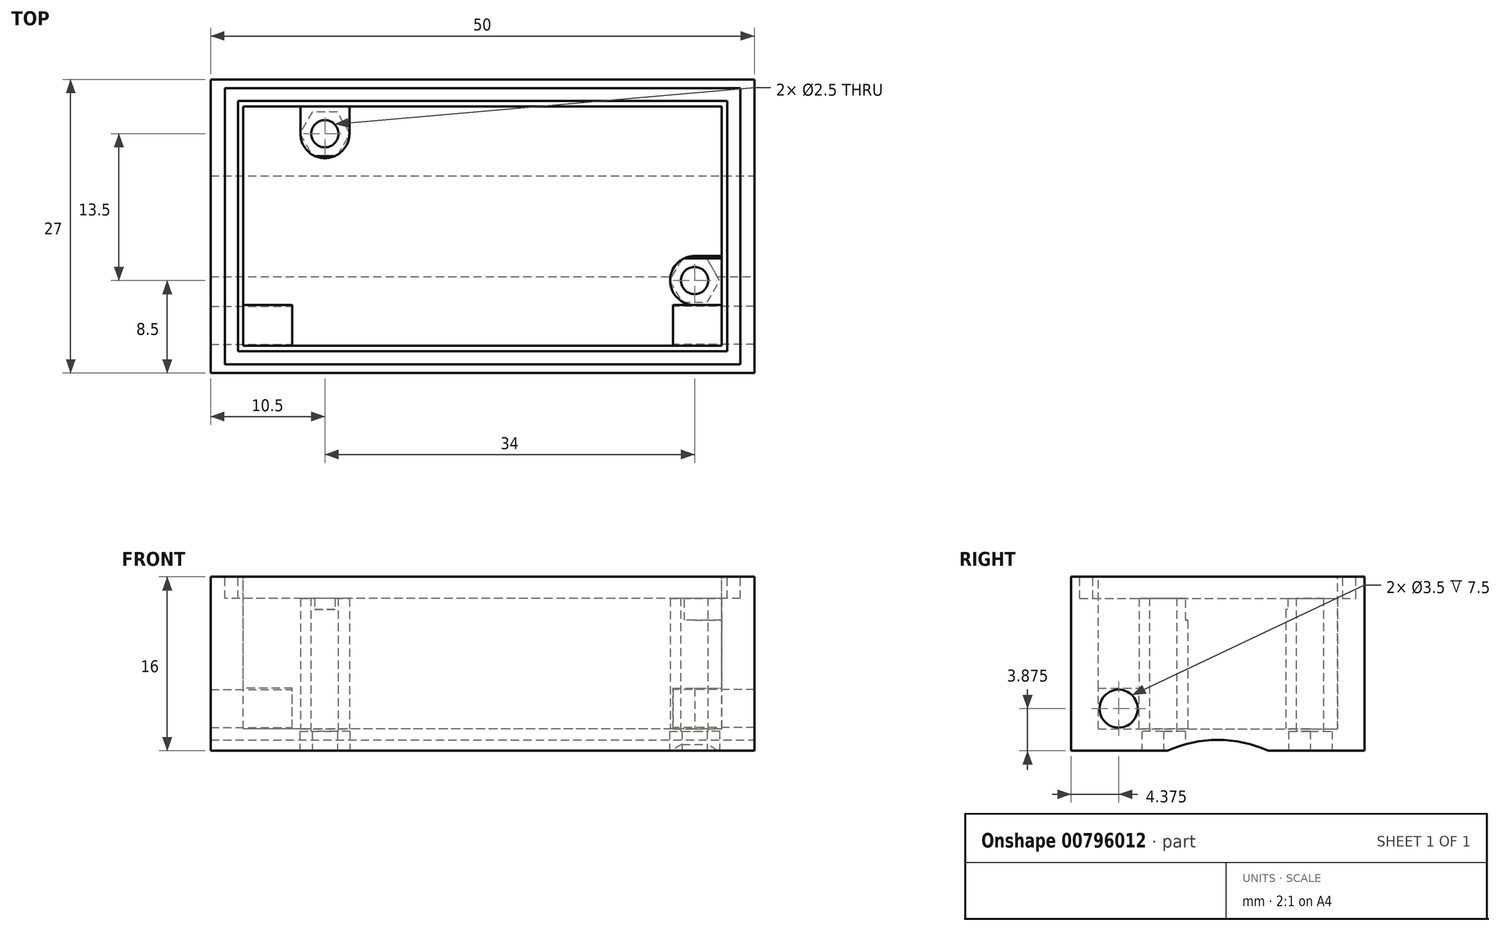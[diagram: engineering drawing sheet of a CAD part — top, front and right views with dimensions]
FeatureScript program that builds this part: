
annotation { "Feature Type Name" : "Feature", "Feature Type Description" : "" }
export const myFeature = defineFeature(function(context is Context, id is Id, definition is map)
    precondition{}
    {
        {
            var Q0;
            Q0=qCreatedBy(makeId("Top.planeOp"),FACE);
            var sketch = newSketch(context, id + "F0", { "sketchPlane" : qUnion([Q0])});
            skLineSegment(sketch, "E0.bottom", {"start": v(25, -13.5) * mm, "end": v(-25, -13.5) * mm});
            skLineSegment(sketch, "E0.top", {"start": v(25, 13.5) * mm, "end": v(-25, 13.5) * mm});
            skLineSegment(sketch, "E0.left", {"start": v(25, -13.5) * mm, "end": v(25, 13.5) * mm});
            skLineSegment(sketch, "E0.right", {"start": v(-25, -13.5) * mm, "end": v(-25, 13.5) * mm});
            skPoint(sketch, "E0.middle", {"position": v(0, 0) * mm});
            skSolve(sketch);
        }
        {
            var Q0;
            Q0 = qSketchRegion(id + "F0", true);
            extrude(context, id + "F1", {"entities" : qUnion([Q0]), "depth" : 16 * mm, "offsetDistance" : 25 * mm});
        }
        {
            var Q0;
            Q0=makeQuery(id+"F1.opExtrude","CAP_FACE",FACE,{"disambiguationData":[OSD([sQuery(id+"F0.wireOp",EDGE,"E0.bottom"),sQuery(id+"F0.wireOp",EDGE,"E0.top"),sQuery(id+"F0.wireOp",EDGE,"E0.left"),sQuery(id+"F0.wireOp",EDGE,"E0.right")])],"isStart":false});
            var sketch = newSketch(context, id + "F2", { "sketchPlane" : qUnion([Q0])});
            skLineSegment(sketch, "E1.bottom", {"start": v(22, -11) * mm, "end": v(-22, -11) * mm});
            skLineSegment(sketch, "E1.top", {"start": v(22, 11) * mm, "end": v(-22, 11) * mm});
            skLineSegment(sketch, "E1.left", {"start": v(22, -11) * mm, "end": v(22, 11) * mm});
            skLineSegment(sketch, "E1.right", {"start": v(-22, -11) * mm, "end": v(-22, 11) * mm});
            skPoint(sketch, "E1.middle", {"position": v(0, 0) * mm});
            skSolve(sketch);
        }
        {
            var Q0;
            Q0 = qSketchRegion(id + "F2", true);
            extrude(context, id + "F3", {"entities" : qUnion([Q0]), "operationType" : NewBodyOperationType.REMOVE, "oppositeDirection" : true, "depth" : 14 * mm, "offsetDistance" : 25 * mm});
        }
        {
            var Q0;
            Q0=makeQuery(id+"F3.boolean.opBoolean","COPY",FACE,{"derivedFrom":makeQuery(id+"F3.opExtrude","CAP_FACE",FACE,{"disambiguationData":[OSD([sQuery(id+"F2.wireOp",EDGE,"E1.bottom"),sQuery(id+"F2.wireOp",EDGE,"E1.top"),sQuery(id+"F2.wireOp",EDGE,"E1.left"),sQuery(id+"F2.wireOp",EDGE,"E1.right")])],"isStart":false})});
            var sketch = newSketch(context, id + "F4", { "sketchPlane" : qUnion([Q0])});
            skCircle(sketch, "E2", {"center": v(19.5, -5) * mm, "radius": 2.25 * mm});
            skCircle(sketch, "E3", {"center": v(-14.5, 8.5) * mm, "radius": 2.25 * mm});
            skLineSegment(sketch, "E4.bottom", {"start": v(-16.75, 8.5) * mm, "end": v(-12.25, 8.5) * mm});
            skLineSegment(sketch, "E4.top", {"start": v(-16.75, 11) * mm, "end": v(-12.25, 11) * mm});
            skLineSegment(sketch, "E4.left", {"start": v(-16.75, 8.5) * mm, "end": v(-16.75, 11) * mm});
            skLineSegment(sketch, "E4.right", {"start": v(-12.25, 8.5) * mm, "end": v(-12.25, 11) * mm});
            skLineSegment(sketch, "E5.bottom", {"start": v(19.5, -7.25) * mm, "end": v(22, -7.25) * mm});
            skLineSegment(sketch, "E5.top", {"start": v(19.5, -2.75) * mm, "end": v(22, -2.75) * mm});
            skLineSegment(sketch, "E5.left", {"start": v(19.5, -7.25) * mm, "end": v(19.5, -2.75) * mm});
            skLineSegment(sketch, "E5.right", {"start": v(22, -7.25) * mm, "end": v(22, -2.75) * mm});
            skSolve(sketch);
        }
        {
            var Q0;
            Q0 = qSketchRegion(id + "F4", true);
            extrude(context, id + "F5", {"entities" : qUnion([Q0]), "operationType" : NewBodyOperationType.ADD, "depth" : 12 * mm, "offsetDistance" : 25 * mm});
        }
        {
            var Q0;
            Q0=makeQuery(id+"F5.opExtrude","CAP_FACE",FACE,{"disambiguationData":[OSD([sQuery(id+"F4.wireOp",EDGE,"E3"),sQuery(id+"F4.wireOp",EDGE,"E4.top"),sQuery(id+"F4.wireOp",EDGE,"E4.left"),sQuery(id+"F4.wireOp",EDGE,"E4.right")])],"isStart":false});
            var sketch = newSketch(context, id + "F6", { "sketchPlane" : qUnion([Q0])});
            skCircle(sketch, "E6", {"center": v(-14.5, 8.5) * mm, "radius": 1.25 * mm});
            skSolve(sketch);
        }
        {
            var Q0;
            Q0=makeQuery(id+"F5.opExtrude","CAP_FACE",FACE,{"disambiguationData":[OSD([sQuery(id+"F4.wireOp",EDGE,"E2"),sQuery(id+"F4.wireOp",EDGE,"E5.bottom"),sQuery(id+"F4.wireOp",EDGE,"E5.top"),sQuery(id+"F4.wireOp",EDGE,"E5.right")])],"isStart":false});
            var sketch = newSketch(context, id + "F7", { "sketchPlane" : qUnion([Q0])});
            skCircle(sketch, "E7", {"center": v(19.5, -5) * mm, "radius": 1.25 * mm});
            skSolve(sketch);
        }
        {
            var Q0;
            Q0=makeQuery(id+"F6.imprint","IMPRINT",FACE,{"disambiguationData":[TD([[makeQuery(id+"F6.imprint","IMPRINT",EDGE,{"derivedFrom":sQuery(id+"F6.wireOp",EDGE,"E6")}),1.0]])]});
            extrude(context, id + "F8", {"entities" : qUnion([Q0]), "operationType" : NewBodyOperationType.REMOVE, "endBound" : BoundingType.THROUGH_ALL, "oppositeDirection" : true, "depth" : 25 * mm, "offsetDistance" : 25 * mm});
        }
        {
            var Q0;
            Q0 = qSketchRegion(id + "F7", true);
            extrude(context, id + "F9", {"entities" : qUnion([Q0]), "operationType" : NewBodyOperationType.REMOVE, "endBound" : BoundingType.THROUGH_ALL, "oppositeDirection" : true, "depth" : 25 * mm, "offsetDistance" : 25 * mm});
        }
        {
            var Q0;
            Q0=makeQuery(id+"F1.opExtrude","CAP_FACE",FACE,{"disambiguationData":[OSD([sQuery(id+"F0.wireOp",EDGE,"E0.bottom"),sQuery(id+"F0.wireOp",EDGE,"E0.top"),sQuery(id+"F0.wireOp",EDGE,"E0.left"),sQuery(id+"F0.wireOp",EDGE,"E0.right")])],"isStart":true});
            var sketch = newSketch(context, id + "F10", { "sketchPlane" : qUnion([Q0])});
            skCircle(sketch, "E8.cCircle", {"center": v(-14.5, -8.5) * mm, "radius": 2 * mm, "construction": true});
            skLineSegment(sketch, "E8.0", {"start": v(-13.35, -10.5) * mm, "end": v(-15.65, -10.5) * mm});
            skLineSegment(sketch, "E8.1", {"start": v(-15.65, -10.5) * mm, "end": v(-16.8, -8.5) * mm});
            skLineSegment(sketch, "E8.2", {"start": v(-16.8, -8.5) * mm, "end": v(-15.65, -6.5) * mm});
            skLineSegment(sketch, "E8.3", {"start": v(-15.65, -6.5) * mm, "end": v(-13.35, -6.5) * mm});
            skLineSegment(sketch, "E8.4", {"start": v(-13.35, -6.5) * mm, "end": v(-12.2, -8.5) * mm});
            skLineSegment(sketch, "E8.5", {"start": v(-12.2, -8.5) * mm, "end": v(-13.35, -10.5) * mm});
            skPoint(sketch, "E8.0.midPoint", {"position": v(-14.5, -10.5) * mm});
            skCircle(sketch, "E9.cCircle", {"center": v(19.5, 5) * mm, "radius": 2 * mm, "construction": true});
            skLineSegment(sketch, "E9.0", {"start": v(18.35, 7) * mm, "end": v(20.65, 7) * mm});
            skLineSegment(sketch, "E9.1", {"start": v(20.65, 7) * mm, "end": v(21.8, 5) * mm});
            skLineSegment(sketch, "E9.2", {"start": v(21.8, 5) * mm, "end": v(20.65, 3) * mm});
            skLineSegment(sketch, "E9.3", {"start": v(20.65, 3) * mm, "end": v(18.35, 3) * mm});
            skLineSegment(sketch, "E9.4", {"start": v(18.35, 3) * mm, "end": v(17.2, 5) * mm});
            skLineSegment(sketch, "E9.5", {"start": v(17.2, 5) * mm, "end": v(18.35, 7) * mm});
            skPoint(sketch, "E9.0.midPoint", {"position": v(19.5, 7) * mm});
            skSolve(sketch);
        }
        {
            var Q0;
            Q0 = qSketchRegion(id + "F10", true);
            extrude(context, id + "F11", {"entities" : qUnion([Q0]), "operationType" : NewBodyOperationType.REMOVE, "oppositeDirection" : true, "depth" : 1.8 * mm, "offsetDistance" : 25 * mm});
        }
        {
            var Q0;
            Q0=makeQuery(id+"F5.opExtrude","CAP_FACE",FACE,{"disambiguationData":[OSD([sQuery(id+"F4.wireOp",EDGE,"E2"),sQuery(id+"F4.wireOp",EDGE,"E5.bottom"),sQuery(id+"F4.wireOp",EDGE,"E5.top"),sQuery(id+"F4.wireOp",EDGE,"E5.right")])],"isStart":false});
            var sketch = newSketch(context, id + "F12", { "sketchPlane" : qUnion([Q0])});
            skLineSegment(sketch, "E10.bottom", {"start": v(22, -2.75) * mm, "end": v(18, -2.75) * mm});
            skLineSegment(sketch, "E10.top", {"start": v(22, -2.95) * mm, "end": v(18, -2.95) * mm});
            skLineSegment(sketch, "E10.left", {"start": v(22, -2.75) * mm, "end": v(22, -2.95) * mm});
            skLineSegment(sketch, "E10.right", {"start": v(18, -2.75) * mm, "end": v(18, -2.95) * mm});
            skSolve(sketch);
        }
        {
            var Q0;
            {var subQ3=sQuery(id+"F12.wireOp",EDGE,"E10.left");Q0=makeQuery(id+"F12.imprint","IMPRINT",FACE,{"disambiguationData":[TD([[makeQuery(id+"F12.imprint","IMPRINT",EDGE,{"derivedFrom":subQ3}),1.0]])]});}
            extrude(context, id + "F13", {"entities" : qUnion([Q0]), "operationType" : NewBodyOperationType.REMOVE, "oppositeDirection" : true, "depth" : 2 * mm, "offsetDistance" : 25 * mm});
        }
        {
            var Q0;
            Q0=makeQuery(id+"F5.opExtrude","CAP_FACE",FACE,{"disambiguationData":[OSD([sQuery(id+"F4.wireOp",EDGE,"E3"),sQuery(id+"F4.wireOp",EDGE,"E4.top"),sQuery(id+"F4.wireOp",EDGE,"E4.left"),sQuery(id+"F4.wireOp",EDGE,"E4.right")])],"isStart":false});
            var sketch = newSketch(context, id + "F14", { "sketchPlane" : qUnion([Q0])});
            skLineSegment(sketch, "E11.bottom", {"start": v(-12.25, 6.25) * mm, "end": v(-16.25, 6.25) * mm});
            skLineSegment(sketch, "E11.top", {"start": v(-12.25, 6.45) * mm, "end": v(-16.25, 6.45) * mm});
            skLineSegment(sketch, "E11.left", {"start": v(-12.25, 6.25) * mm, "end": v(-12.25, 6.45) * mm});
            skLineSegment(sketch, "E11.right", {"start": v(-16.25, 6.25) * mm, "end": v(-16.25, 6.45) * mm});
            skPoint(sketch, "E11.middle", {"position": v(-14.25, 6.35) * mm});
            skSolve(sketch);
        }
        {
            var Q0;
            Q0 = qSketchRegion(id + "F14", true);
            extrude(context, id + "F15", {"entities" : qUnion([Q0]), "operationType" : NewBodyOperationType.REMOVE, "oppositeDirection" : true, "depth" : 1 * mm, "offsetDistance" : 25 * mm});
        }
        {
            var Q0;
            Q0=makeQuery(id+"F1.opExtrude","CAP_FACE",FACE,{"disambiguationData":[OSD([sQuery(id+"F0.wireOp",EDGE,"E0.bottom"),sQuery(id+"F0.wireOp",EDGE,"E0.top"),sQuery(id+"F0.wireOp",EDGE,"E0.left"),sQuery(id+"F0.wireOp",EDGE,"E0.right")])],"isStart":false});
            var sketch = newSketch(context, id + "F16", { "sketchPlane" : qUnion([Q0])});
            skLineSegment(sketch, "E12.bottom", {"start": v(-22.5, -12) * mm, "end": v(-23.7, -12) * mm});
            skLineSegment(sketch, "E12.top", {"start": v(-22.5, 12) * mm, "end": v(-23.7, 12) * mm});
            skLineSegment(sketch, "E12.left", {"start": v(-22.5, -12) * mm, "end": v(-22.5, 12) * mm});
            skLineSegment(sketch, "E12.right", {"start": v(-23.7, -12) * mm, "end": v(-23.7, 12) * mm});
            skPoint(sketch, "E12.middle", {"position": v(-23.1, 0) * mm});
            skLineSegment(sketch, "E13.bottom", {"start": v(23.7, -12) * mm, "end": v(22.5, -12) * mm});
            skLineSegment(sketch, "E13.top", {"start": v(23.7, 12) * mm, "end": v(22.5, 12) * mm});
            skLineSegment(sketch, "E13.left", {"start": v(23.7, -12) * mm, "end": v(23.7, 12) * mm});
            skLineSegment(sketch, "E13.right", {"start": v(22.5, -12) * mm, "end": v(22.5, 12) * mm});
            skPoint(sketch, "E13.middle", {"position": v(23.1, 0) * mm});
            skLineSegment(sketch, "E14.bottom", {"start": v(23.7, -12.7) * mm, "end": v(-23.7, -12.7) * mm});
            skLineSegment(sketch, "E14.top", {"start": v(23.7, -11.5) * mm, "end": v(-23.7, -11.5) * mm});
            skLineSegment(sketch, "E14.left", {"start": v(23.7, -12.7) * mm, "end": v(23.7, -11.5) * mm});
            skLineSegment(sketch, "E14.right", {"start": v(-23.7, -12.7) * mm, "end": v(-23.7, -11.5) * mm});
            skPoint(sketch, "E14.middle", {"position": v(0, -12.1) * mm});
            skLineSegment(sketch, "E15.bottom", {"start": v(23.7, 11.5) * mm, "end": v(-23.7, 11.5) * mm});
            skLineSegment(sketch, "E15.top", {"start": v(23.7, 12.7) * mm, "end": v(-23.7, 12.7) * mm});
            skLineSegment(sketch, "E15.left", {"start": v(23.7, 11.5) * mm, "end": v(23.7, 12.7) * mm});
            skLineSegment(sketch, "E15.right", {"start": v(-23.7, 11.5) * mm, "end": v(-23.7, 12.7) * mm});
            skPoint(sketch, "E15.middle", {"position": v(0, 12.1) * mm});
            skSolve(sketch);
        }
        {
            var Q0;
            Q0 = qSketchRegion(id + "F16", true);
            extrude(context, id + "F17", {"entities" : qUnion([Q0]), "operationType" : NewBodyOperationType.REMOVE, "oppositeDirection" : true, "depth" : 2 * mm, "offsetDistance" : 25 * mm});
        }
        {
            var Q0;
            Q0=makeQuery(id+"F13.boolean.opBoolean","MERGE",FACE,{"derivedFrom":[makeQuery(id+"F3.boolean.opBoolean","COPY",FACE,{"derivedFrom":makeQuery(id+"F3.opExtrude","SWEPT_FACE",FACE,{"disambiguationData":[OSD([sQuery(id+"F2.wireOp",EDGE,"E1.left")])]})}),makeQuery(id+"F13.opExtrude","SWEPT_FACE",FACE,{"disambiguationData":[OSD([sQuery(id+"F12.wireOp",EDGE,"E10.left")])]})]});
            var sketch = newSketch(context, id + "F18", { "sketchPlane" : qUnion([Q0])});
            skLineSegment(sketch, "E16.bottom", {"start": v(11, 2) * mm, "end": v(7.25, 2) * mm});
            skLineSegment(sketch, "E16.top", {"start": v(11, 5.75) * mm, "end": v(7.25, 5.75) * mm});
            skLineSegment(sketch, "E16.left", {"start": v(11, 2) * mm, "end": v(11, 5.75) * mm});
            skLineSegment(sketch, "E16.right", {"start": v(7.25, 2) * mm, "end": v(7.25, 5.75) * mm});
            skPoint(sketch, "E16.middle", {"position": v(9.12, 3.88) * mm});
            skSolve(sketch);
        }
        {
            var Q0;
            Q0 = qSketchRegion(id + "F18", true);
            extrude(context, id + "F19", {"entities" : qUnion([Q0]), "operationType" : NewBodyOperationType.ADD, "depth" : 4.5 * mm, "offsetDistance" : 25 * mm});
        }
        {
            var Q0;
            Q0=makeQuery(id+"F3.boolean.opBoolean","COPY",FACE,{"derivedFrom":makeQuery(id+"F3.opExtrude","SWEPT_FACE",FACE,{"disambiguationData":[OSD([sQuery(id+"F2.wireOp",EDGE,"E1.right")])]})});
            var sketch = newSketch(context, id + "F20", { "sketchPlane" : qUnion([Q0])});
            skLineSegment(sketch, "E17.bottom", {"start": v(-11, 2) * mm, "end": v(-7.25, 2) * mm});
            skLineSegment(sketch, "E17.top", {"start": v(-11, 5.75) * mm, "end": v(-7.25, 5.75) * mm});
            skLineSegment(sketch, "E17.left", {"start": v(-11, 2) * mm, "end": v(-11, 5.75) * mm});
            skLineSegment(sketch, "E17.right", {"start": v(-7.25, 2) * mm, "end": v(-7.25, 5.75) * mm});
            skSolve(sketch);
        }
        {
            var Q0;
            Q0 = qSketchRegion(id + "F20", true);
            extrude(context, id + "F21", {"entities" : qUnion([Q0]), "operationType" : NewBodyOperationType.ADD, "depth" : 4.5 * mm, "offsetDistance" : 25 * mm});
        }
        {
            var Q0;
            Q0=makeQuery(id+"F21.opExtrude","CAP_FACE",FACE,{"disambiguationData":[OSD([sQuery(id+"F20.wireOp",EDGE,"E17.bottom"),sQuery(id+"F20.wireOp",EDGE,"E17.top"),sQuery(id+"F20.wireOp",EDGE,"E17.left"),sQuery(id+"F20.wireOp",EDGE,"E17.right")])],"isStart":false});
            var sketch = newSketch(context, id + "F22", { "sketchPlane" : qUnion([Q0])});
            skCircle(sketch, "E18", {"center": v(-9.13, 3.88) * mm, "radius": 1.75 * mm});
            skPoint(sketch, "E18.centerSnap0", {"position": v(-7.25, 3.88) * mm});
            skPoint(sketch, "E18.centerSnap1", {"position": v(-9.13, 5.75) * mm});
            skSolve(sketch);
        }
        {
            var Q0;
            Q0 = qSketchRegion(id + "F22", true);
            extrude(context, id + "F23", {"entities" : qUnion([Q0]), "operationType" : NewBodyOperationType.REMOVE, "endBound" : BoundingType.THROUGH_ALL, "oppositeDirection" : true, "depth" : 25 * mm, "offsetDistance" : 25 * mm});
        }
        {
            var Q0;
            Q0=makeQuery(id+"F19.opExtrude","CAP_FACE",FACE,{"disambiguationData":[OSD([sQuery(id+"F18.wireOp",EDGE,"E16.bottom"),sQuery(id+"F18.wireOp",EDGE,"E16.top"),sQuery(id+"F18.wireOp",EDGE,"E16.left"),sQuery(id+"F18.wireOp",EDGE,"E16.right")])],"isStart":false});
            var sketch = newSketch(context, id + "F24", { "sketchPlane" : qUnion([Q0])});
            skCircle(sketch, "E19", {"center": v(9.12, 3.88) * mm, "radius": 1.75 * mm});
            skPoint(sketch, "E19.centerSnap0", {"position": v(7.25, 3.88) * mm});
            skPoint(sketch, "E19.centerSnap1", {"position": v(9.12, 5.75) * mm});
            skSolve(sketch);
        }
        {
            var Q0;
            Q0 = qSketchRegion(id + "F24", true);
            extrude(context, id + "F25", {"entities" : qUnion([Q0]), "operationType" : NewBodyOperationType.REMOVE, "endBound" : BoundingType.THROUGH_ALL, "oppositeDirection" : true, "depth" : 25 * mm, "offsetDistance" : 25 * mm});
        }
        {
            var Q0;
            Q0=qCreatedBy(makeId("Right.planeOp"),FACE);
            var sketch = newSketch(context, id + "F26", { "sketchPlane" : qUnion([Q0])});
            skCircle(sketch, "E20", {"center": v(0, -10.25) * mm, "radius": 11.25 * mm});
            skSolve(sketch);
        }
        {
            var Q0;
            Q0 = qSketchRegion(id + "F26", true);
            extrude(context, id + "F27", {"entities" : qUnion([Q0]), "operationType" : NewBodyOperationType.REMOVE, "endBound" : BoundingType.SYMMETRIC, "oppositeDirection" : true, "depth" : 59 * mm, "offsetDistance" : 25 * mm});
        }
    });
